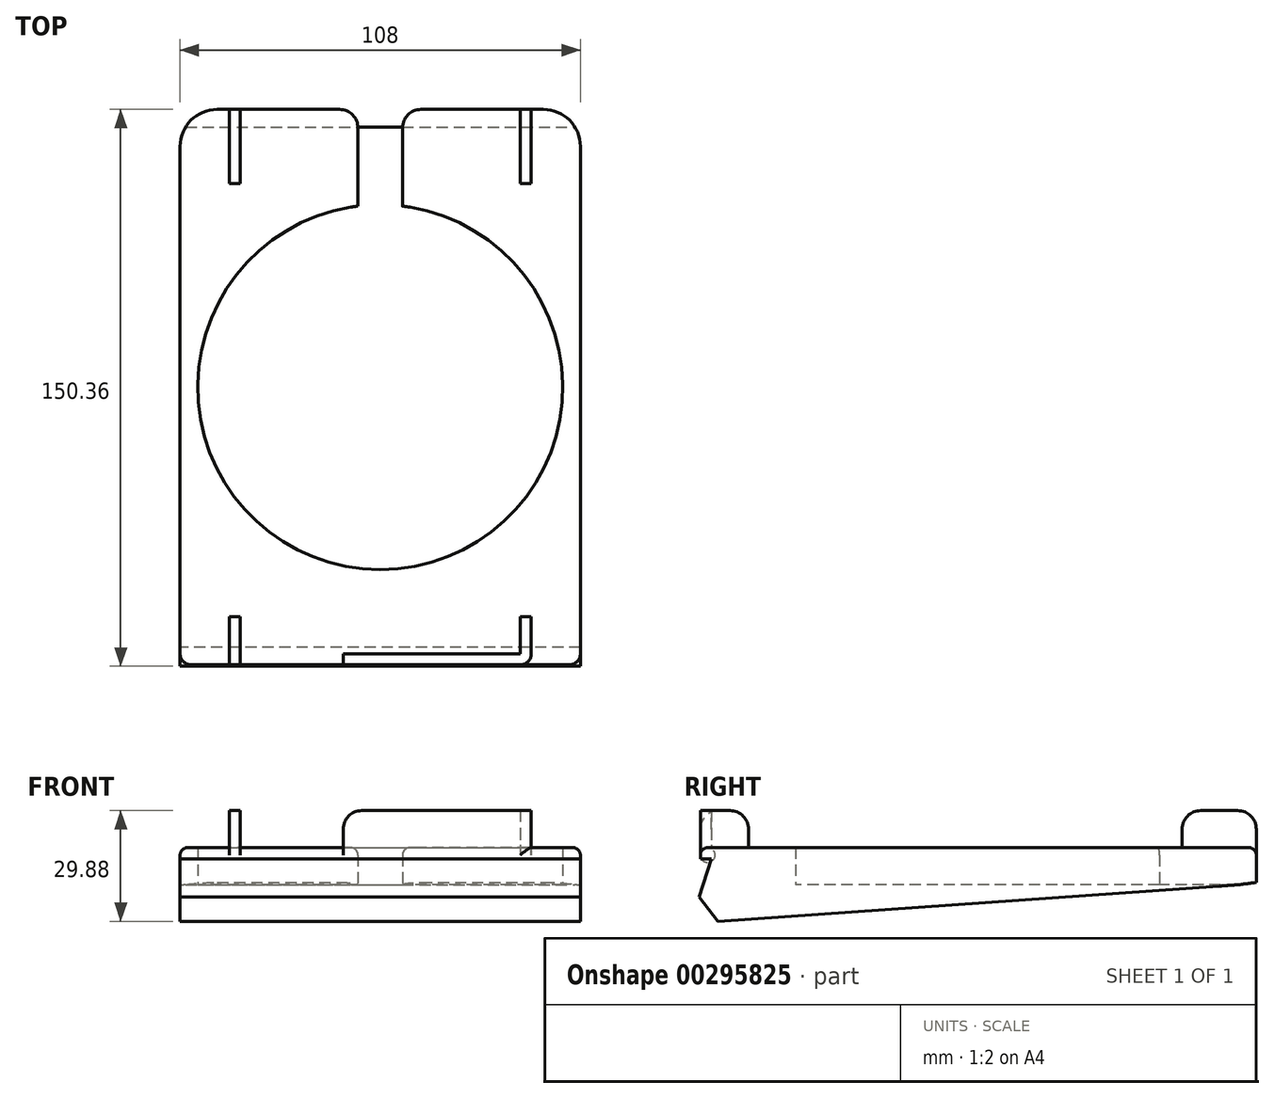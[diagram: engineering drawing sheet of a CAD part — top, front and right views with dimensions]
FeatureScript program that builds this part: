
annotation { "Feature Type Name" : "Feature", "Feature Type Description" : "" }
export const myFeature = defineFeature(function(context is Context, id is Id, definition is map)
    precondition{}
    {
        {
            var Q0;
            Q0=qCreatedBy(makeId("Top.planeOp"),FACE);
            var sketch = newSketch(context, id + "F0", { "sketchPlane" : qUnion([Q0])});
            skLineSegment(sketch, "E0.bottom", {"start": v(-30.49, 108.13) * mm, "end": v(17.51, 108.13) * mm});
            skLineSegment(sketch, "E0.top", {"start": v(-30.49, -41.87) * mm, "end": v(77.51, -41.87) * mm});
            skLineSegment(sketch, "E0.left", {"start": v(-30.49, 108.13) * mm, "end": v(-30.49, -41.87) * mm});
            skLineSegment(sketch, "E0.right", {"start": v(77.51, 108.13) * mm, "end": v(77.51, -41.87) * mm});
            skArc(sketch, "E1", {"start": v(17.51, 82.02) * mm, "mid": v(23.51, -16.12) * mm, "end": v(29.51, 82.02) * mm});
            skLineSegment(sketch, "E2", {"start": v(29.51, 108.13) * mm, "end": v(29.51, 82.02) * mm});
            skLineSegment(sketch, "E3", {"start": v(17.51, 108.13) * mm, "end": v(17.51, 82.02) * mm});
            skLineSegment(sketch, "E4.trimOffspring", {"start": v(29.51, 108.13) * mm, "end": v(77.51, 108.13) * mm});
            skPoint(sketch, "E5.orphan", {"position": v(23.51, 108.13) * mm});
            skPoint(sketch, "E6.end.orphan", {"position": v(23.51, -41.87) * mm});
            skSolve(sketch);
        }
        {
            var Q0;
            Q0=makeQuery(id+"F0.imprint","IMPRINT",FACE,{"disambiguationData":[TD([[makeQuery(id+"F0.imprint","IMPRINT",EDGE,{"derivedFrom":sQuery(id+"F0.wireOp",EDGE,"E0.bottom")}),-1.0]])]});
            extrude(context, id + "F1", {"entities" : qUnion([Q0]), "depth" : 10 * mm});
        }
        {
            var Q0;
            Q0=makeQuery(id+"F1.opExtrude","CAP_FACE",FACE,{"disambiguationData":[OSD([sQuery(id+"F0.wireOp",EDGE,"E0.bottom"),sQuery(id+"F0.wireOp",EDGE,"E0.top"),sQuery(id+"F0.wireOp",EDGE,"E0.left"),sQuery(id+"F0.wireOp",EDGE,"E0.right"),sQuery(id+"F0.wireOp",EDGE,"E1"),sQuery(id+"F0.wireOp",EDGE,"E2"),sQuery(id+"F0.wireOp",EDGE,"E3"),sQuery(id+"F0.wireOp",EDGE,"E4.trimOffspring")])],"isStart":false});
            var sketch = newSketch(context, id + "F2", { "sketchPlane" : qUnion([Q0])});
            skLineSegment(sketch, "E7", {"start": v(23.51, -41.87) * mm, "end": v(61.26, -41.87) * mm});
            skLineSegment(sketch, "E8", {"start": v(23.51, -41.87) * mm, "end": v(13.51, -41.87) * mm});
            skLineSegment(sketch, "E9", {"start": v(13.51, -41.87) * mm, "end": v(13.51, -38.87) * mm});
            skLineSegment(sketch, "E10", {"start": v(61.26, -41.87) * mm, "end": v(61.26, -38.87) * mm});
            skLineSegment(sketch, "E11", {"start": v(13.51, -38.87) * mm, "end": v(61.26, -38.87) * mm});
            skLineSegment(sketch, "E12", {"start": v(77.51, 108.13) * mm, "end": v(64.26, 108.13) * mm});
            skLineSegment(sketch, "E13", {"start": v(64.26, 108.13) * mm, "end": v(64.26, 88.13) * mm});
            skLineSegment(sketch, "E14", {"start": v(64.26, 88.13) * mm, "end": v(61.26, 88.13) * mm});
            skLineSegment(sketch, "E15", {"start": v(61.26, 88.13) * mm, "end": v(61.26, 108.13) * mm});
            skLineSegment(sketch, "E16", {"start": v(-30.49, 108.13) * mm, "end": v(-17.24, 108.13) * mm});
            skLineSegment(sketch, "E17", {"start": v(-17.24, 108.13) * mm, "end": v(-17.24, 88.13) * mm});
            skLineSegment(sketch, "E18", {"start": v(-17.24, 88.13) * mm, "end": v(-14.24, 88.13) * mm});
            skLineSegment(sketch, "E19", {"start": v(-14.24, 88.13) * mm, "end": v(-14.24, 108.13) * mm});
            skLineSegment(sketch, "E20", {"start": v(61.26, -38.87) * mm, "end": v(61.26, -28.87) * mm});
            skLineSegment(sketch, "E21", {"start": v(61.26, -28.87) * mm, "end": v(64.26, -28.87) * mm});
            skLineSegment(sketch, "E22", {"start": v(64.26, -28.87) * mm, "end": v(64.26, -41.87) * mm});
            skLineSegment(sketch, "E23", {"start": v(-30.49, -41.87) * mm, "end": v(-17.24, -41.87) * mm});
            skLineSegment(sketch, "E24", {"start": v(-17.24, -41.87) * mm, "end": v(-17.24, -28.87) * mm});
            skLineSegment(sketch, "E25", {"start": v(-17.24, -28.87) * mm, "end": v(-14.24, -28.87) * mm});
            skLineSegment(sketch, "E26", {"start": v(-14.24, -28.87) * mm, "end": v(-14.24, -41.87) * mm});
            skSolve(sketch);
        }
        {
            var Q0;
            Q0=makeQuery(id+"F2.imprint","IMPRINT",FACE,{"disambiguationData":[TD([[makeQuery(id+"F2.imprint","IMPRINT",EDGE,{"derivedFrom":sQuery(id+"F2.wireOp",EDGE,"E7")}),1.0]])]});
            extrude(context, id + "F3", {"entities" : qUnion([Q0]), "operationType" : NewBodyOperationType.ADD, "depth" : 10 * mm});
        }
        {
            var Q0;
            Q0=makeQuery(id+"F1.opExtrude","SWEPT_FACE",FACE,{"disambiguationData":[OSD([sQuery(id+"F0.wireOp",EDGE,"E0.right")])]});
            var sketch = newSketch(context, id + "F4", { "sketchPlane" : qUnion([Q0])});
            skLineSegment(sketch, "E27", {"start": v(-41.87, 10) * mm, "end": v(-41.87, 7) * mm});
            skLineSegment(sketch, "E28", {"start": v(-41.87, 7) * mm, "end": v(-38.87, 7) * mm});
            skLineSegment(sketch, "E29", {"start": v(-41.87, 7) * mm, "end": v(-41.87, 0) * mm});
            skLineSegment(sketch, "E30", {"start": v(-41.87, 0) * mm, "end": v(-36.6, 0) * mm});
            skLineSegment(sketch, "E31", {"start": v(108.13, 0) * mm, "end": v(103.38, 0) * mm});
            skLineSegment(sketch, "E32", {"start": v(-36.6, 0) * mm, "end": v(103.38, 0) * mm});
            skLineSegment(sketch, "E33", {"start": v(103.38, 0) * mm, "end": v(108.13, 0.62) * mm});
            skLineSegment(sketch, "E34", {"start": v(103.38, 0) * mm, "end": v(-44.52, -10.4) * mm});
            skLineSegment(sketch, "E35", {"start": v(-44.52, -10.4) * mm, "end": v(-38.87, 7) * mm});
            skLineSegment(sketch, "E36", {"start": v(-38.87, 7) * mm, "end": v(-38.87, 0) * mm});
            skSolve(sketch);
        }
        {
            var Q0;
            Q0=makeQuery(id+"F4.imprint","IMPRINT",FACE,{"disambiguationData":[TD([[makeQuery(id+"F4.imprint","IMPRINT",EDGE,{"derivedFrom":sQuery(id+"F4.wireOp",EDGE,"E28")}),-1.0]])]});
            var Q1;
            {var subQ0=sQuery(id+"F4.wireOp",EDGE,"sKtt6eXu-lU7I-tQr0-vSHH-LqeA10OcXJb4");Q1=makeQuery(id+"F4.imprint","IMPRINT",FACE,{"disambiguationData":[TD([[makeQuery(id+"F4.imprint","IMPRINT",EDGE,{"derivedFrom":subQ0}),-1.0]])]});}
            extrude(context, id + "F5", {"entities" : qUnion([Q0, Q1]), "operationType" : NewBodyOperationType.REMOVE, "oppositeDirection" : true, "depth" : 112.1 * mm});
        }
        {
            var Q0;
            {var subQ0=sQuery(id+"F4.wireOp",EDGE,"E31");Q0=makeQuery(id+"F4.imprint","IMPRINT",FACE,{"disambiguationData":[TD([[makeQuery(id+"F4.imprint","IMPRINT",EDGE,{"derivedFrom":subQ0}),-1.0]])]});}
            extrude(context, id + "F6", {"entities" : qUnion([Q0]), "operationType" : NewBodyOperationType.REMOVE, "oppositeDirection" : true, "depth" : 112.8 * mm});
        }
        {
            var Q0;
            {var subQ0=sQuery(id+"F4.wireOp",EDGE,"E34");Q0=makeQuery(id+"F4.imprint","IMPRINT",FACE,{"disambiguationData":[TD([[makeQuery(id+"F4.imprint","IMPRINT",EDGE,{"derivedFrom":subQ0}),-1.0]])]});}
            extrude(context, id + "F7", {"entities" : qUnion([Q0]), "operationType" : NewBodyOperationType.ADD, "oppositeDirection" : true, "depth" : 108 * mm});
        }
        {
            var Q0;
            {var subQ0=sQuery(id+"F2.wireOp",EDGE,"E17");Q0=makeQuery(id+"F2.imprint","IMPRINT",FACE,{"disambiguationData":[TD([[makeQuery(id+"F2.imprint","IMPRINT",EDGE,{"derivedFrom":subQ0}),1.0]])]});}
            var Q1;
            {var subQ0=sQuery(id+"F2.wireOp",EDGE,"E13");Q1=makeQuery(id+"F2.imprint","IMPRINT",FACE,{"disambiguationData":[TD([[makeQuery(id+"F2.imprint","IMPRINT",EDGE,{"derivedFrom":subQ0}),-1.0]])]});}
            var Q2;
            {var subQ0=sQuery(id+"F2.wireOp",EDGE,"E24");Q2=makeQuery(id+"F2.imprint","IMPRINT",FACE,{"disambiguationData":[TD([[makeQuery(id+"F2.imprint","IMPRINT",EDGE,{"derivedFrom":subQ0}),-1.0]])]});}
            var Q3;
            {var subQ1=sQuery(id+"F2.wireOp",EDGE,"E10");Q3=makeQuery(id+"F2.imprint","IMPRINT",FACE,{"disambiguationData":[TD([[makeQuery(id+"F2.imprint","IMPRINT",EDGE,{"derivedFrom":subQ1}),-1.0]])]});}
            extrude(context, id + "F8", {"entities" : qUnion([Q0, Q1, Q2, Q3]), "operationType" : NewBodyOperationType.ADD, "depth" : 10 * mm});
        }
        {
            var Q0;
            Q0=makeQuery(id+"F1.opExtrude","SWEPT_EDGE",EDGE,{"disambiguationData":[OSD([sQuery(id+"F0.wireOp",EDGE,"E0.bottom"),sQuery(id+"F0.wireOp",EDGE,"E3")])]});
            var Q1;
            Q1=makeQuery(id+"F1.opExtrude","SWEPT_EDGE",EDGE,{"disambiguationData":[OSD([sQuery(id+"F0.wireOp",EDGE,"E2"),sQuery(id+"F0.wireOp",EDGE,"E4.trimOffspring")])]});
            fillet(context, id + "F9", {"entities" : qUnion([Q0, Q1]), "radius" : 5 * mm, "tangentPropagation" : true, "allowEdgeOverflow" : false});
        }
        {
            var Q0;
            Q0=makeQuery(id+"F1.opExtrude","SWEPT_EDGE",EDGE,{"disambiguationData":[OSD([sQuery(id+"F0.wireOp",EDGE,"E0.right"),sQuery(id+"F0.wireOp",EDGE,"E4.trimOffspring")])]});
            var Q1;
            Q1=makeQuery(id+"F1.opExtrude","SWEPT_EDGE",EDGE,{"disambiguationData":[OSD([sQuery(id+"F0.wireOp",EDGE,"E0.bottom"),sQuery(id+"F0.wireOp",EDGE,"E0.left")])]});
            fillet(context, id + "F10", {"entities" : qUnion([Q0, Q1]), "radius" : 10 * mm, "tangentPropagation" : true, "allowEdgeOverflow" : false});
        }
        {
            var Q0;
            Q0=makeQuery(id+"F8.opExtrude","CAP_EDGE",EDGE,{"disambiguationData":[OSD([sQuery(id+"F2.wireOp",EDGE,"E18")])],"isStart":false});
            var Q1;
            Q1=makeQuery(id+"F8.opExtrude","CAP_EDGE",EDGE,{"disambiguationData":[OSD([sQuery(id+"F0.wireOp",EDGE,"E0.bottom")])],"isStart":false});
            var Q2;
            Q2=makeQuery(id+"F8.opExtrude","CAP_EDGE",EDGE,{"disambiguationData":[OSD([sQuery(id+"F2.wireOp",EDGE,"E14")])],"isStart":false});
            var Q3;
            Q3=makeQuery(id+"F8.opExtrude","CAP_EDGE",EDGE,{"disambiguationData":[OSD([sQuery(id+"F0.wireOp",EDGE,"E4.trimOffspring")])],"isStart":false});
            var Q4;
            Q4=makeQuery(id+"F8.opExtrude","CAP_EDGE",EDGE,{"disambiguationData":[OSD([sQuery(id+"F2.wireOp",EDGE,"E21")])],"isStart":false});
            var Q5;
            Q5=makeQuery(id+"F8.opExtrude","CAP_EDGE",EDGE,{"disambiguationData":[OSD([sQuery(id+"F2.wireOp",EDGE,"E25")])],"isStart":false});
            var Q6;
            {var subQ0=sQuery(id+"F0.wireOp",EDGE,"E0.top");var subQ1=makeQuery(id+"F1.opExtrude","CAP_EDGE",EDGE,{"disambiguationData":[OSD([subQ0])],"isStart":false});Q6=makeQuery(id+"F8.opExtrude","CAP_EDGE",EDGE,{"disambiguationData":[OSD([subQ0]),TDD([makeQuery(id+"F2.imprint","IMPRINT",EDGE,{"disambiguationData":[TD([[makeQuery(id+"F2.imprint","INTERSECT",VERTEX,{"derivedFrom":[subQ1,sQuery(id+"F2.wireOp",EDGE,"E26")]}),1.0]])],"derivedFrom":subQ1})])],"isStart":false});}
            var Q7;
            Q7=makeQuery(id+"F3.opExtrude","CAP_EDGE",EDGE,{"disambiguationData":[OSD([sQuery(id+"F2.wireOp",EDGE,"E9")])],"isStart":false});
            fillet(context, id + "F11", {"entities" : qUnion([Q0, Q1, Q2, Q3, Q4, Q5, Q6, Q7]), "radius" : 5 * mm, "tangentPropagation" : true, "allowEdgeOverflow" : false});
        }
        {
            var Q0;
            Q0=makeQuery(id+"F1.opExtrude","CAP_EDGE",EDGE,{"disambiguationData":[OSD([sQuery(id+"F0.wireOp",EDGE,"E0.right")])],"isStart":false});
            var Q1;
            {var subQ0=sQuery(id+"F0.wireOp",EDGE,"E0.right");var subQ1=sQuery(id+"F0.wireOp",EDGE,"E0.top");Q1=makeQuery(id+"F10.opFillet","BLEND_EDGE",EDGE,{"blendedFrom":[makeQuery(id+"F1.opExtrude","SWEPT_EDGE",EDGE,{"disambiguationData":[OSD([subQ1,subQ0])]}),makeQuery(id+"F1.opExtrude","CAP_FACE",FACE,{"disambiguationData":[OSD([sQuery(id+"F0.wireOp",EDGE,"E0.bottom"),subQ1,sQuery(id+"F0.wireOp",EDGE,"E0.left"),subQ0,sQuery(id+"F0.wireOp",EDGE,"E1"),sQuery(id+"F0.wireOp",EDGE,"E2"),sQuery(id+"F0.wireOp",EDGE,"E3"),sQuery(id+"F0.wireOp",EDGE,"E4.trimOffspring")])],"isStart":false})],"blendedInto":[makeQuery(id+"F1.opExtrude","CAP_FACE",FACE,{"disambiguationData":[OSD([sQuery(id+"F0.wireOp",EDGE,"E0.bottom"),subQ1,sQuery(id+"F0.wireOp",EDGE,"E0.left"),subQ0,sQuery(id+"F0.wireOp",EDGE,"E1"),sQuery(id+"F0.wireOp",EDGE,"E2"),sQuery(id+"F0.wireOp",EDGE,"E3"),sQuery(id+"F0.wireOp",EDGE,"E4.trimOffspring")])],"isStart":false})]});}
            var Q2;
            {var subQ0=makeQuery(id+"F3.opExtrude","SWEPT_FACE",FACE,{"disambiguationData":[OSD([sQuery(id+"F2.wireOp",EDGE,"E9")])]});var subQ3=sQuery(id+"F0.wireOp",EDGE,"E0.top");var subQ5=sQuery(id+"F0.wireOp",EDGE,"E0.left");var subQ8=makeQuery(id+"F1.opExtrude","CAP_EDGE",EDGE,{"disambiguationData":[OSD([subQ3])],"isStart":false});Q2=makeQuery(id+"F8.boolean.opBoolean","SPLIT",EDGE,{"disambiguationData":[TD([subQ0])],"derivedFrom":makeQuery(id+"F3.boolean.opBoolean","SPLIT",EDGE,{"disambiguationData":[TD([makeQuery(id+"F1.opExtrude","SWEPT_FACE",FACE,{"disambiguationData":[OSD([subQ5])]})])],"derivedFrom":subQ8})});}
            var Q3;
            {var subQ0=sQuery(id+"F0.wireOp",EDGE,"E0.right");var subQ1=sQuery(id+"F0.wireOp",EDGE,"E0.top");Q3=makeQuery(id+"F3.boolean.opBoolean","SPLIT",EDGE,{"disambiguationData":[TD([makeQuery(id+"F1.opExtrude","SWEPT_FACE",FACE,{"disambiguationData":[OSD([subQ0])]})])],"derivedFrom":makeQuery(id+"F1.opExtrude","CAP_EDGE",EDGE,{"disambiguationData":[OSD([subQ1])],"isStart":false})});}
            var Q4;
            {var subQ0=sQuery(id+"F0.wireOp",EDGE,"E0.left");var subQ1=makeQuery(id+"F1.opExtrude","SWEPT_FACE",FACE,{"disambiguationData":[OSD([subQ0])]});var subQ5=sQuery(id+"F0.wireOp",EDGE,"E0.top");var subQ8=makeQuery(id+"F1.opExtrude","CAP_EDGE",EDGE,{"disambiguationData":[OSD([subQ5])],"isStart":false});Q4=makeQuery(id+"F8.boolean.opBoolean","SPLIT",EDGE,{"disambiguationData":[TD([subQ1])],"derivedFrom":makeQuery(id+"F3.boolean.opBoolean","SPLIT",EDGE,{"disambiguationData":[TD([subQ1])],"derivedFrom":subQ8})});}
            var Q5;
            {var subQ0=sQuery(id+"F0.wireOp",EDGE,"E0.left");var subQ1=sQuery(id+"F0.wireOp",EDGE,"E0.top");Q5=makeQuery(id+"F10.opFillet","BLEND_EDGE",EDGE,{"blendedFrom":[makeQuery(id+"F1.opExtrude","SWEPT_EDGE",EDGE,{"disambiguationData":[OSD([subQ1,subQ0])]}),makeQuery(id+"F1.opExtrude","CAP_FACE",FACE,{"disambiguationData":[OSD([sQuery(id+"F0.wireOp",EDGE,"E0.bottom"),subQ1,subQ0,sQuery(id+"F0.wireOp",EDGE,"E0.right"),sQuery(id+"F0.wireOp",EDGE,"E1"),sQuery(id+"F0.wireOp",EDGE,"E2"),sQuery(id+"F0.wireOp",EDGE,"E3"),sQuery(id+"F0.wireOp",EDGE,"E4.trimOffspring")])],"isStart":false})],"blendedInto":[makeQuery(id+"F1.opExtrude","CAP_FACE",FACE,{"disambiguationData":[OSD([sQuery(id+"F0.wireOp",EDGE,"E0.bottom"),subQ1,subQ0,sQuery(id+"F0.wireOp",EDGE,"E0.right"),sQuery(id+"F0.wireOp",EDGE,"E1"),sQuery(id+"F0.wireOp",EDGE,"E2"),sQuery(id+"F0.wireOp",EDGE,"E3"),sQuery(id+"F0.wireOp",EDGE,"E4.trimOffspring")])],"isStart":false})]});}
            var Q6;
            Q6=makeQuery(id+"F1.opExtrude","CAP_EDGE",EDGE,{"disambiguationData":[OSD([sQuery(id+"F0.wireOp",EDGE,"E0.left")])],"isStart":false});
            var Q7;
            {var subQ0=sQuery(id+"F0.wireOp",EDGE,"E0.left");var subQ1=sQuery(id+"F0.wireOp",EDGE,"E0.bottom");Q7=makeQuery(id+"F10.opFillet","BLEND_EDGE",EDGE,{"blendedFrom":[makeQuery(id+"F1.opExtrude","SWEPT_EDGE",EDGE,{"disambiguationData":[OSD([subQ1,subQ0])]}),makeQuery(id+"F1.opExtrude","CAP_FACE",FACE,{"disambiguationData":[OSD([subQ1,sQuery(id+"F0.wireOp",EDGE,"E0.top"),subQ0,sQuery(id+"F0.wireOp",EDGE,"E0.right"),sQuery(id+"F0.wireOp",EDGE,"E1"),sQuery(id+"F0.wireOp",EDGE,"E2"),sQuery(id+"F0.wireOp",EDGE,"E3"),sQuery(id+"F0.wireOp",EDGE,"E4.trimOffspring")])],"isStart":false})],"blendedInto":[makeQuery(id+"F1.opExtrude","CAP_FACE",FACE,{"disambiguationData":[OSD([subQ1,sQuery(id+"F0.wireOp",EDGE,"E0.top"),subQ0,sQuery(id+"F0.wireOp",EDGE,"E0.right"),sQuery(id+"F0.wireOp",EDGE,"E1"),sQuery(id+"F0.wireOp",EDGE,"E2"),sQuery(id+"F0.wireOp",EDGE,"E3"),sQuery(id+"F0.wireOp",EDGE,"E4.trimOffspring")])],"isStart":false})]});}
            var Q8;
            {var subQ0=sQuery(id+"F0.wireOp",EDGE,"E0.left");var subQ1=sQuery(id+"F0.wireOp",EDGE,"E0.bottom");Q8=makeQuery(id+"F8.boolean.opBoolean","SPLIT",EDGE,{"disambiguationData":[TD([makeQuery(id+"F1.opExtrude","SWEPT_FACE",FACE,{"disambiguationData":[OSD([subQ0])]})])],"derivedFrom":makeQuery(id+"F1.opExtrude","CAP_EDGE",EDGE,{"disambiguationData":[OSD([subQ1])],"isStart":false})});}
            var Q9;
            {var subQ0=sQuery(id+"F0.wireOp",EDGE,"E3");var subQ1=sQuery(id+"F0.wireOp",EDGE,"E0.bottom");Q9=makeQuery(id+"F8.boolean.opBoolean","SPLIT",EDGE,{"disambiguationData":[TD([makeQuery(id+"F1.opExtrude","SWEPT_FACE",FACE,{"disambiguationData":[OSD([subQ0])]})])],"derivedFrom":makeQuery(id+"F1.opExtrude","CAP_EDGE",EDGE,{"disambiguationData":[OSD([subQ1])],"isStart":false})});}
            var Q10;
            {var subQ0=sQuery(id+"F0.wireOp",EDGE,"E4.trimOffspring");var subQ1=sQuery(id+"F0.wireOp",EDGE,"E2");Q10=makeQuery(id+"F8.boolean.opBoolean","SPLIT",EDGE,{"disambiguationData":[TD([makeQuery(id+"F1.opExtrude","SWEPT_FACE",FACE,{"disambiguationData":[OSD([subQ1])]})])],"derivedFrom":makeQuery(id+"F1.opExtrude","CAP_EDGE",EDGE,{"disambiguationData":[OSD([subQ0])],"isStart":false})});}
            var Q11;
            {var subQ0=sQuery(id+"F0.wireOp",EDGE,"E4.trimOffspring");var subQ1=sQuery(id+"F0.wireOp",EDGE,"E0.right");Q11=makeQuery(id+"F10.opFillet","BLEND_EDGE",EDGE,{"blendedFrom":[makeQuery(id+"F1.opExtrude","SWEPT_EDGE",EDGE,{"disambiguationData":[OSD([subQ1,subQ0])]}),makeQuery(id+"F1.opExtrude","CAP_FACE",FACE,{"disambiguationData":[OSD([sQuery(id+"F0.wireOp",EDGE,"E0.bottom"),sQuery(id+"F0.wireOp",EDGE,"E0.top"),sQuery(id+"F0.wireOp",EDGE,"E0.left"),subQ1,sQuery(id+"F0.wireOp",EDGE,"E1"),sQuery(id+"F0.wireOp",EDGE,"E2"),sQuery(id+"F0.wireOp",EDGE,"E3"),subQ0])],"isStart":false})],"blendedInto":[makeQuery(id+"F1.opExtrude","CAP_FACE",FACE,{"disambiguationData":[OSD([sQuery(id+"F0.wireOp",EDGE,"E0.bottom"),sQuery(id+"F0.wireOp",EDGE,"E0.top"),sQuery(id+"F0.wireOp",EDGE,"E0.left"),subQ1,sQuery(id+"F0.wireOp",EDGE,"E1"),sQuery(id+"F0.wireOp",EDGE,"E2"),sQuery(id+"F0.wireOp",EDGE,"E3"),subQ0])],"isStart":false})]});}
            var Q12;
            {var subQ0=sQuery(id+"F0.wireOp",EDGE,"E4.trimOffspring");var subQ1=sQuery(id+"F0.wireOp",EDGE,"E0.right");Q12=makeQuery(id+"F8.boolean.opBoolean","SPLIT",EDGE,{"disambiguationData":[TD([makeQuery(id+"F1.opExtrude","SWEPT_FACE",FACE,{"disambiguationData":[OSD([subQ1])]})])],"derivedFrom":makeQuery(id+"F1.opExtrude","CAP_EDGE",EDGE,{"disambiguationData":[OSD([subQ0])],"isStart":false})});}
            fillet(context, id + "F12", {"entities" : qUnion([Q0, Q1, Q2, Q3, Q4, Q5, Q6, Q7, Q8, Q9, Q10, Q11, Q12]), "radius" : 2 * mm, "tangentPropagation" : true, "allowEdgeOverflow" : false});
        }
        {
            var Q0;
            Q0=makeQuery(id+"F8.opExtrude","SWEPT_EDGE",EDGE,{"disambiguationData":[OSD([sQuery(id+"F0.wireOp",EDGE,"E0.top"),sQuery(id+"F2.wireOp",EDGE,"E22")])]});
            var Q1;
            Q1=makeQuery(id+"F3.opExtrude","SWEPT_EDGE",EDGE,{"disambiguationData":[OSD([sQuery(id+"F2.wireOp",EDGE,"E10"),sQuery(id+"F2.wireOp",EDGE,"E11"),sQuery(id+"F2.wireOp",EDGE,"E20")])]});
            fillet(context, id + "F13", {"entities" : qUnion([Q0, Q1]), "radius" : 3 * mm, "tangentPropagation" : true, "allowEdgeOverflow" : false});
        }
        {
            var Q0;
            Q0=makeQuery(id+"F1.opExtrude","SWEPT_EDGE",EDGE,{"disambiguationData":[OSD([sQuery(id+"F0.wireOp",EDGE,"E0.top"),sQuery(id+"F0.wireOp",EDGE,"E0.right")])]});
            var Q1;
            Q1=makeQuery(id+"F1.opExtrude","SWEPT_EDGE",EDGE,{"disambiguationData":[OSD([sQuery(id+"F0.wireOp",EDGE,"E0.top"),sQuery(id+"F0.wireOp",EDGE,"E0.left")])]});
            fillet(context, id + "F14", {"entities" : qUnion([Q0, Q1]), "radius" : 3 * mm, "tangentPropagation" : true, "allowEdgeOverflow" : false});
        }
        {
            var Q0;
            Q0=makeQuery(id+"F7.opExtrude","SWEPT_EDGE",EDGE,{"disambiguationData":[OSD([sQuery(id+"F4.wireOp",EDGE,"E34"),sQuery(id+"F4.wireOp",EDGE,"E35")])]});
            chamfer(context, id + "F15", {"entities" : qUnion([Q0]), "width" : 5 * mm, "tangentPropagation" : true});
        }
    });
